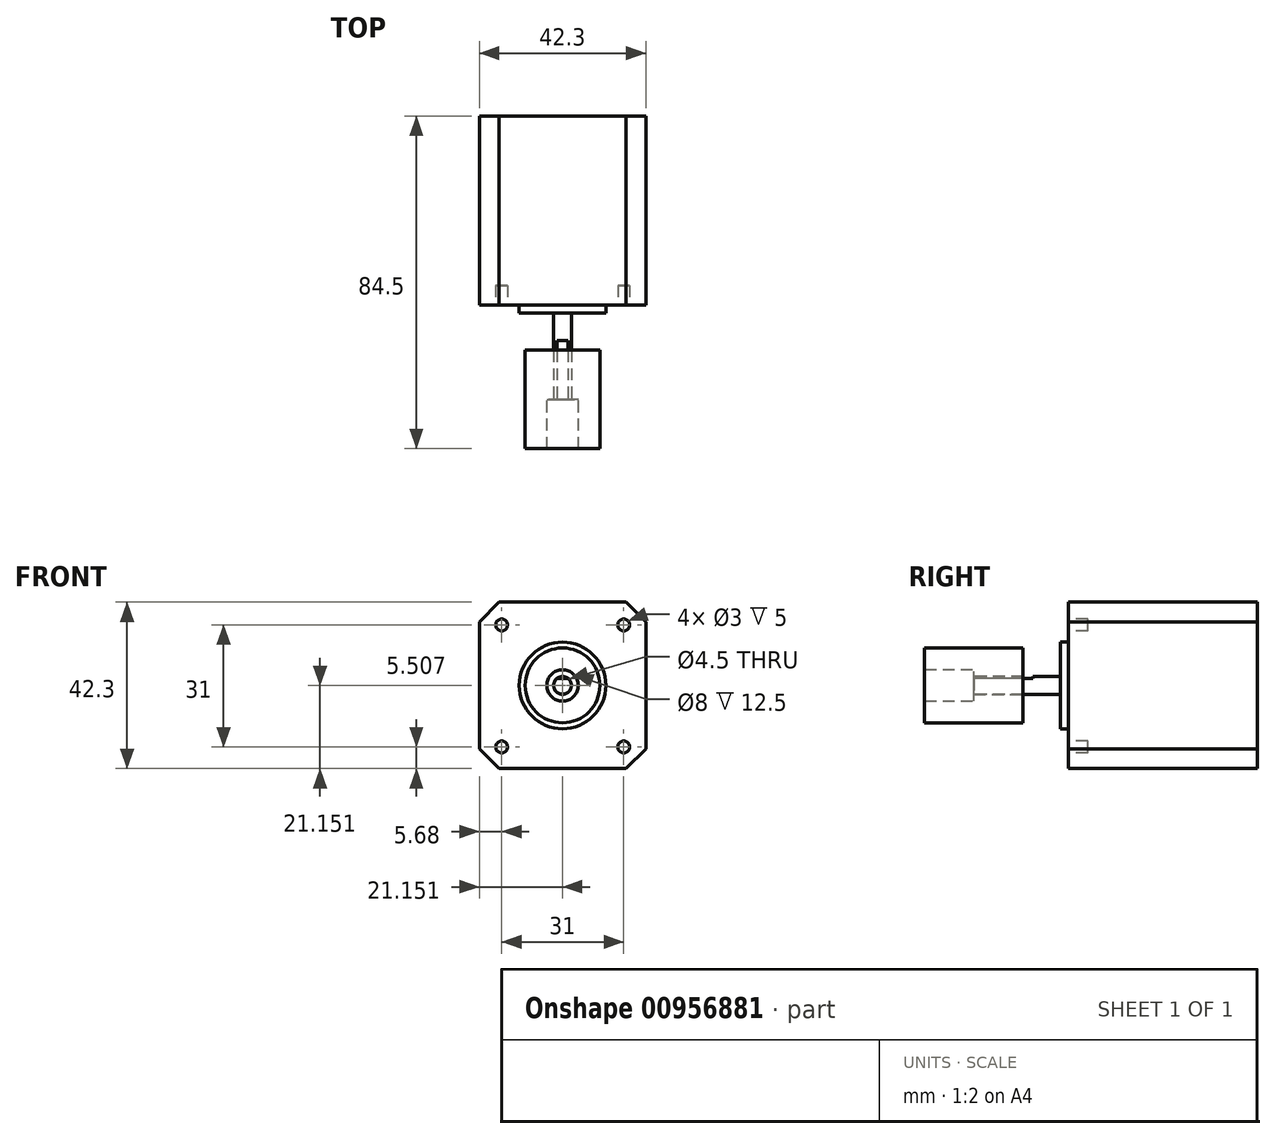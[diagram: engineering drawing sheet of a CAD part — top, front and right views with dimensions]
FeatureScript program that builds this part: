
annotation { "Feature Type Name" : "Feature", "Feature Type Description" : "" }
export const myFeature = defineFeature(function(context is Context, id is Id, definition is map)
    precondition{}
    {
        {
            var Q0;
            Q0=qCreatedBy(makeId("Front.planeOp"),FACE);
            var sketch = newSketch(context, id + "F0", { "sketchPlane" : qUnion([Q0])});
            skLineSegment(sketch, "E0.bottom", {"start": v(3.78, -2.56) * mm, "end": v(46.08, -2.56) * mm});
            skLineSegment(sketch, "E0.top", {"start": v(3.78, -44.86) * mm, "end": v(46.08, -44.86) * mm});
            skLineSegment(sketch, "E0.left", {"start": v(3.78, -2.56) * mm, "end": v(3.78, -44.86) * mm});
            skLineSegment(sketch, "E0.right", {"start": v(46.08, -2.56) * mm, "end": v(46.08, -44.86) * mm});
            skCircle(sketch, "E1", {"center": v(24.93, -23.7) * mm, "radius": 11 * mm});
            skPoint(sketch, "E2.orphan", {"position": v(46.08, -23.7) * mm});
            skPoint(sketch, "E3.orphan", {"position": v(24.93, -2.56) * mm});
            skPoint(sketch, "E4.orphan", {"position": v(3.78, -23.7) * mm});
            skPoint(sketch, "E5.end.orphan", {"position": v(24.93, -44.86) * mm});
            skCircle(sketch, "E6", {"center": v(24.93, -23.7) * mm, "radius": 2.25 * mm});
            skSolve(sketch);
        }
        {
            var Q0;
            Q0 = qSketchRegion(id + "F0", true);
            var Q1;
            Q1=makeQuery(id+"F0.imprint","IMPRINT",FACE,{"disambiguationData":[TD([[makeQuery(id+"F0.imprint","IMPRINT",EDGE,{"derivedFrom":sQuery(id+"F0.wireOp",EDGE,"E1")}),1.0]])]});
            var Q2;
            Q2=makeQuery(id+"F0.imprint","IMPRINT",FACE,{"disambiguationData":[TD([[makeQuery(id+"F0.imprint","IMPRINT",EDGE,{"derivedFrom":sQuery(id+"F0.wireOp",EDGE,"E6")}),1.0]])]});
            extrude(context, id + "F1", {"entities" : qUnion([Q0, Q1, Q2]), "oppositeDirection" : true, "depth" : 48 * mm, "offsetDistance" : 25 * mm});
        }
        {
            var Q0;
            Q0=makeQuery(id+"F0.imprint","IMPRINT",FACE,{"disambiguationData":[TD([[makeQuery(id+"F0.imprint","IMPRINT",EDGE,{"derivedFrom":sQuery(id+"F0.wireOp",EDGE,"E1")}),1.0]])]});
            extrude(context, id + "F2", {"entities" : qUnion([Q0]), "operationType" : NewBodyOperationType.ADD, "depth" : 2 * mm, "offsetDistance" : 25 * mm});
        }
        {
            var Q0;
            Q0=makeQuery(id+"F0.imprint","IMPRINT",FACE,{"disambiguationData":[TD([[makeQuery(id+"F0.imprint","IMPRINT",EDGE,{"derivedFrom":sQuery(id+"F0.wireOp",EDGE,"E6")}),1.0]])]});
            extrude(context, id + "F3", {"entities" : qUnion([Q0]), "operationType" : NewBodyOperationType.ADD, "depth" : 24 * mm, "offsetDistance" : 25 * mm});
        }
        {
            var Q0;
            Q0=makeQuery(id+"F1.opExtrude","SWEPT_EDGE",EDGE,{"disambiguationData":[OSD([sQuery(id+"F0.wireOp",EDGE,"E0.bottom"),sQuery(id+"F0.wireOp",EDGE,"E0.right")])]});
            var Q1;
            Q1=makeQuery(id+"F1.opExtrude","SWEPT_EDGE",EDGE,{"disambiguationData":[OSD([sQuery(id+"F0.wireOp",EDGE,"E0.bottom"),sQuery(id+"F0.wireOp",EDGE,"E0.left")])]});
            var Q2;
            Q2=makeQuery(id+"F1.opExtrude","SWEPT_EDGE",EDGE,{"disambiguationData":[OSD([sQuery(id+"F0.wireOp",EDGE,"E0.top"),sQuery(id+"F0.wireOp",EDGE,"E0.right")])]});
            var Q3;
            Q3=makeQuery(id+"F1.opExtrude","SWEPT_EDGE",EDGE,{"disambiguationData":[OSD([sQuery(id+"F0.wireOp",EDGE,"E0.top"),sQuery(id+"F0.wireOp",EDGE,"E0.left")])]});
            chamfer(context, id + "F4", {"entities" : qUnion([Q0, Q1, Q2, Q3]), "width" : 5 * mm, "tangentPropagation" : true});
        }
        {
            var Q0;
            Q0=makeQuery(id+"F0.imprint","IMPRINT",FACE,{"disambiguationData":[TD([[makeQuery(id+"F0.imprint","IMPRINT",EDGE,{"derivedFrom":sQuery(id+"F0.wireOp",EDGE,"E0.bottom")}),-1.0]])]});
            var sketch = newSketch(context, id + "F5", { "sketchPlane" : qUnion([Q0])});
            skLineSegment(sketch, "E7.bottom", {"start": v(40.46, -39.35) * mm, "end": v(9.46, -39.35) * mm, "construction": true});
            skLineSegment(sketch, "E7.top", {"start": v(40.46, -8.35) * mm, "end": v(9.46, -8.35) * mm, "construction": true});
            skLineSegment(sketch, "E7.left", {"start": v(40.46, -39.35) * mm, "end": v(40.46, -8.35) * mm, "construction": true});
            skLineSegment(sketch, "E7.right", {"start": v(9.46, -39.35) * mm, "end": v(9.46, -8.35) * mm, "construction": true});
            skPoint(sketch, "E7.middle", {"position": v(24.96, -23.85) * mm});
            skCircle(sketch, "E8", {"center": v(9.46, -8.35) * mm, "radius": 1.5 * mm});
            skCircle(sketch, "E9", {"center": v(40.46, -8.35) * mm, "radius": 1.5 * mm});
            skCircle(sketch, "E10", {"center": v(9.46, -39.35) * mm, "radius": 1.5 * mm});
            skCircle(sketch, "E11", {"center": v(40.46, -39.35) * mm, "radius": 1.5 * mm});
            skSolve(sketch);
        }
        {
            var Q0;
            Q0 = qSketchRegion(id + "F5", true);
            extrude(context, id + "F6", {"entities" : qUnion([Q0]), "operationType" : NewBodyOperationType.REMOVE, "oppositeDirection" : true, "depth" : 5 * mm, "offsetDistance" : 25 * mm});
        }
        {
            var Q0;
            Q0=makeQuery(id+"F3.opExtrude","CAP_FACE",FACE,{"disambiguationData":[OSD([sQuery(id+"F0.wireOp",EDGE,"E6")])],"isStart":false});
            var sketch = newSketch(context, id + "F7", { "sketchPlane" : qUnion([Q0])});
            skLineSegment(sketch, "E12", {"start": v(23.52, -21.96) * mm, "end": v(26.35, -21.96) * mm});
            skLineSegment(sketch, "E13", {"start": v(24.93, -21.96) * mm, "end": v(24.93, -21.46) * mm, "construction": true});
            skSolve(sketch);
        }
        {
            var Q0;
            {var subQ0=sQuery(id+"F7.wireOp",EDGE,"E12");Q0=makeQuery(id+"F7.imprint","IMPRINT",FACE,{"disambiguationData":[TD([[makeQuery(id+"F7.imprint","IMPRINT",EDGE,{"derivedFrom":subQ0}),1.0]])]});}
            var sketch = newSketch(context, id + "F8", { "sketchPlane" : qUnion([Q0])});
            skSolve(sketch);
        }
        {
            var Q0;
            Q0 = qSketchRegion(id + "F8", true);
            var Q1;
            {var subQ0=sQuery(id+"F7.wireOp",EDGE,"E12");Q1=makeQuery(id+"F8.imprint","IMPRINT",FACE,{"disambiguationData":[TD([[makeQuery(id+"F8.imprint","IMPRINT",EDGE,{"derivedFrom":makeQuery(id+"F7.imprint","IMPRINT",EDGE,{"derivedFrom":subQ0})}),1.0]])]});}
            extrude(context, id + "F9", {"entities" : qUnion([Q0, Q1]), "operationType" : NewBodyOperationType.REMOVE, "oppositeDirection" : true, "depth" : 15 * mm, "offsetDistance" : 25 * mm});
        }
        {
            var Q0;
            {var subQ0=sQuery(id+"F7.wireOp",EDGE,"E12");Q0=makeQuery(id+"F7.imprint","IMPRINT",FACE,{"disambiguationData":[TD([[makeQuery(id+"F7.imprint","IMPRINT",EDGE,{"derivedFrom":subQ0}),-1.0]])]});}
            var sketch = newSketch(context, id + "F10", { "sketchPlane" : qUnion([Q0])});
            skCircle(sketch, "E14.0", {"center": v(24.93, -23.7) * mm, "radius": 2.25 * mm});
            skCircle(sketch, "E15", {"center": v(24.93, -23.7) * mm, "radius": 9.5 * mm});
            skSolve(sketch);
        }
        {
            var Q0;
            Q0 = qSketchRegion(id + "F10", true);
            extrude(context, id + "F11", {"entities" : qUnion([Q0]), "oppositeDirection" : true, "depth" : 12.5 * mm, "offsetDistance" : 25 * mm});
        }
        {
            var Q0;
            Q0=makeQuery(id+"F10.imprint","IMPRINT",FACE,{"disambiguationData":[TD([[makeQuery(id+"F10.imprint","IMPRINT",EDGE,{"derivedFrom":sQuery(id+"F10.wireOp",EDGE,"E15")}),1.0]])]});
            var sketch = newSketch(context, id + "F12", { "sketchPlane" : qUnion([Q0])});
            skCircle(sketch, "E16.0", {"center": v(24.93, -23.7) * mm, "radius": 2.25 * mm});
            skCircle(sketch, "E17", {"center": v(24.93, -23.7) * mm, "radius": 4 * mm});
            skCircle(sketch, "E18.0", {"center": v(24.93, -23.7) * mm, "radius": 9.5 * mm});
            skSolve(sketch);
        }
        {
            var Q0;
            Q0=makeQuery(id+"F12.imprint","IMPRINT",FACE,{"disambiguationData":[TD([[makeQuery(id+"F12.imprint","IMPRINT",EDGE,{"derivedFrom":sQuery(id+"F12.wireOp",EDGE,"E17")}),-1.0]])]});
            extrude(context, id + "F13", {"entities" : qUnion([Q0]), "operationType" : NewBodyOperationType.ADD, "depth" : 12.5 * mm, "offsetDistance" : 25 * mm});
        }
    });
